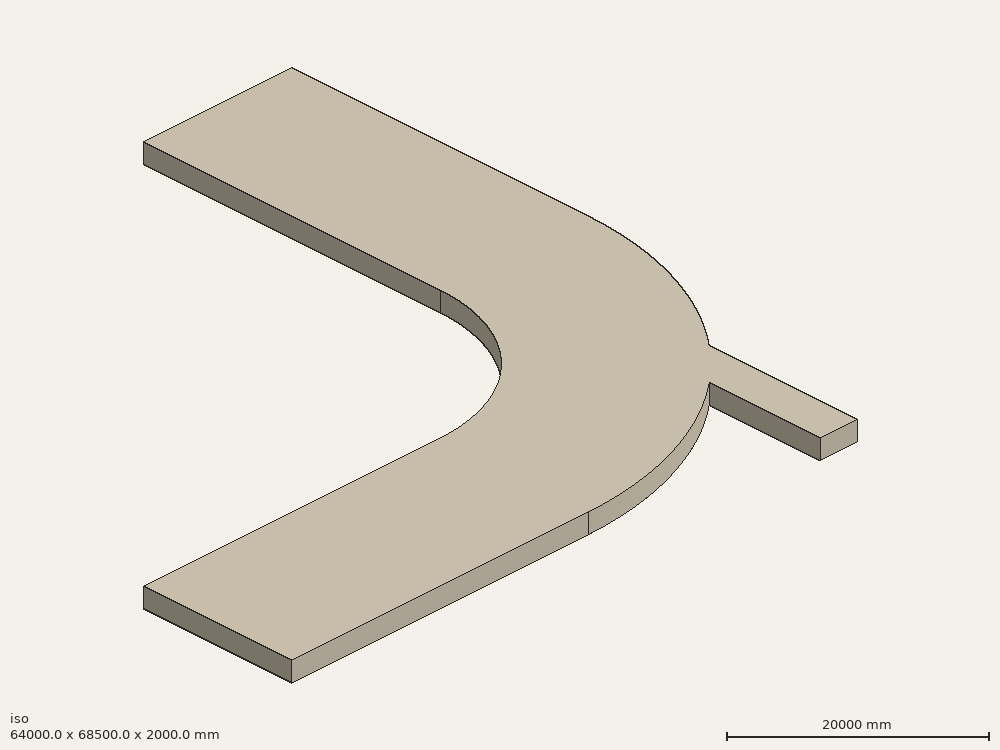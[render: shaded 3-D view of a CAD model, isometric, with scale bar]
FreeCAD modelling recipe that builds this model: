
FCSTD DOCUMENT  (FreeCAD 0.17R10887 (Git))
Label: elbow
License: All rights reserved
LicenseURL: http://en.wikipedia.org/wiki/All_rights_reserved
objects: Sketcher::SketchObject×1, PartDesign::Pad×1
note: 3 computed .brp shape members not serialized (recipe doc carries the construction recipe); baked Part::Feature solids carry a one-line shape summary decoded from their .brp

FEATURE [Sketcher::SketchObject] Sketch
  MapMode = 5
  sketch-geometry (13):
    g0: LineSegment StartX=0 StartY=16000 StartZ=0 EndX=32000 EndY=16000 EndZ=0
    g1: LineSegment StartX=32000 StartY=0 StartZ=0 EndX=0 EndY=0 EndZ=0
    g2: LineSegment StartX=0 StartY=0 StartZ=0 EndX=0 EndY=16000 EndZ=0
    g3: GeomPoint [constr] X=32000 Y=32000 Z=0
    g4: LineSegment StartX=64000 StartY=32000 StartZ=0 EndX=64000 EndY=64000 EndZ=0
    g5: LineSegment StartX=64000 StartY=64000 StartZ=0 EndX=48000 EndY=64000 EndZ=0
    g6: LineSegment StartX=48000 StartY=64000 StartZ=0 EndX=48000 EndY=32000 EndZ=0
    g7: ArcOfCircle CenterX=32000 CenterY=32000 CenterZ=0 NormalX=0 NormalY=0 NormalZ=1 Radius=16000 StartAngle=4.71239 EndAngle=6.28319
    g8: LineSegment StartX=52550 StartY=-4500 StartZ=0 EndX=56550 EndY=-4500 EndZ=0
    g9: LineSegment StartX=52550 StartY=-4500 StartZ=0 EndX=52550 EndY=7470.48 EndZ=0
    g10: LineSegment StartX=56550 StartY=-4500 StartZ=0 EndX=56550 EndY=11474.5 EndZ=0
    g11: ArcOfCircle CenterX=32000 CenterY=32000 CenterZ=0 NormalX=0 NormalY=0 NormalZ=1 Radius=32000 StartAngle=4.71239 EndAngle=5.40974
    g12: ArcOfCircle CenterX=32000 CenterY=32000 CenterZ=0 NormalX=0 NormalY=0 NormalZ=1 Radius=32000 StartAngle=5.58683 EndAngle=6.28319
  constraints (37):
    c: Coincident(g1,g2)
    c: Coincident(g2,g0)
    c: Horizontal(g0)
    c: Horizontal(g1)
    c: Vertical(g2)
    c: DistanceY(g2,g2) = 16000
    c: DistanceX(g1,g1) = 32000
    c: DistanceY(g0,g3) = 16000
    c: DistanceX(g0,g3) = 32000
    c: Coincident(g4,g5)
    c: Coincident(g5,g6)
    c: Horizontal(g5)
    c: Vertical(g4)
    c: Vertical(g6)
    c: DistanceY(g0,g6) = 16000
    c: DistanceX(g0,g6) = 16000
    c: Coincident(g7,g3)
    c: Coincident(g7,g0)
    c: Horizontal(g8)
    c: DistanceX(g1,g8) = 52550
    c: DistanceX(g8,g8) = 4000
    c: DistanceY(g8,g1) = 4500
    c: Coincident(g9,g8)
    c: Vertical(g9)
    c: Coincident(g10,g8)
    c: Coincident(g7,g6)
    c: Coincident(g11,g3)
    c: Coincident(g11,g1)
    c: Coincident(g11,g9)
    c: Coincident(g12,g3)
    c: Coincident(g12,g4)
    c: Radius(g12) = 32000
    c: DistanceY(g4,g4) = 32000
    c: DistanceY(g6,g4) = 0
    c: Parallel(g10,g9)
    c: Coincident(g10,g12)
    c: Coincident(g-1,g1)
FEATURE [PartDesign::Pad] Pad
  Length = 2000
  Length2 = 100
  Profile = -> Sketch
  Type = 0
